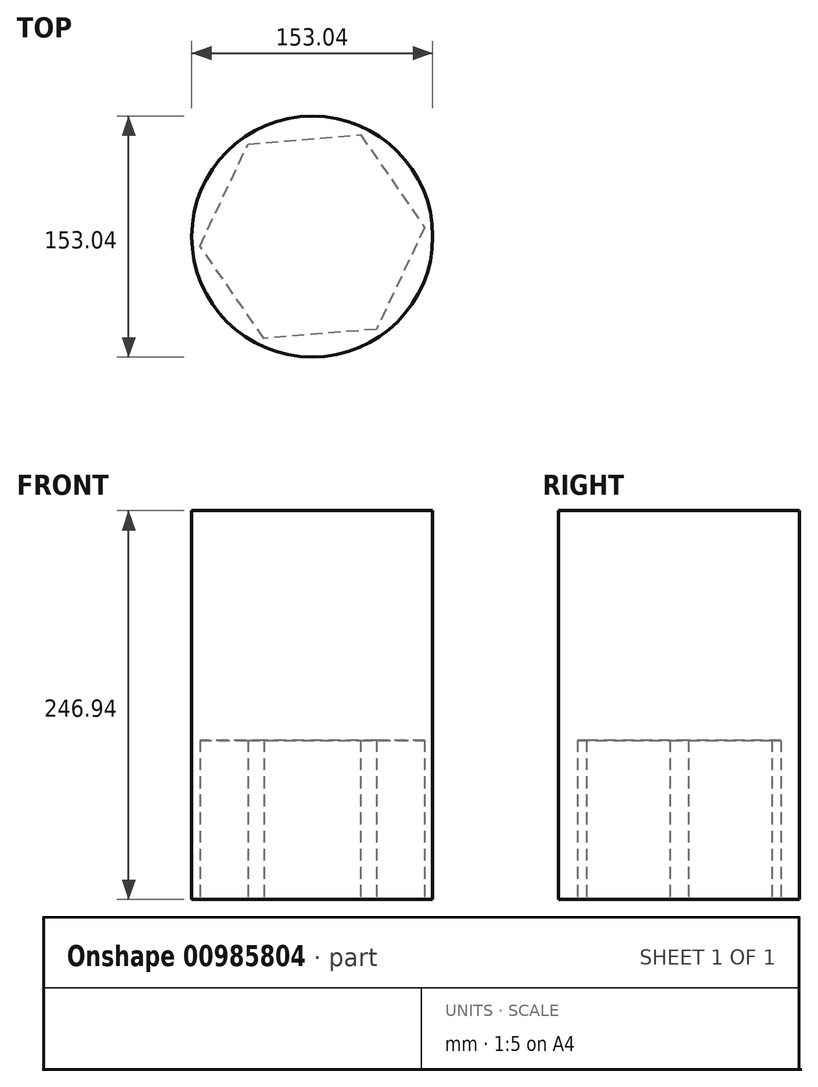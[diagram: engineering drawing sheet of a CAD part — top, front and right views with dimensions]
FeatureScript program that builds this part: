
annotation { "Feature Type Name" : "Feature", "Feature Type Description" : "" }
export const myFeature = defineFeature(function(context is Context, id is Id, definition is map)
    precondition{}
    {
        {
            var Q0;
            Q0=qCreatedBy(makeId("Top.planeOp"),FACE);
            var sketch = newSketch(context, id + "F0", { "sketchPlane" : qUnion([Q0])});
            skCircle(sketch, "E0", {"center": v(0, 0) * mm, "radius": 76.52 * mm});
            skSolve(sketch);
        }
        {
            var Q0;
            Q0=sQuery(id+"F0.wireOp",EDGE,"E0");
            extrude(context, id + "F1", {"bodyType" : ToolBodyType.SURFACE, "surfaceEntities" : qUnion([Q0]), "depth" : 57.15 * mm, "offsetDistance" : 25.4 * mm});
        }
        {
            var Q0;
            Q0=makeQuery(id+"F0.imprint","IMPRINT",FACE,{"disambiguationData":[TD([[makeQuery(id+"F0.imprint","IMPRINT",EDGE,{"derivedFrom":sQuery(id+"F0.wireOp",EDGE,"E0")}),1.0]])]});
            var sketch = newSketch(context, id + "F2", { "sketchPlane" : qUnion([Q0])});
            skCircle(sketch, "E1.cCircle", {"center": v(0, 0) * mm, "radius": 62.03 * mm, "construction": true});
            skLineSegment(sketch, "E1.0", {"start": v(-40.78, 58.89) * mm, "end": v(30.61, 64.76) * mm});
            skLineSegment(sketch, "E1.1", {"start": v(30.61, 64.76) * mm, "end": v(71.39, 5.87) * mm});
            skLineSegment(sketch, "E1.2", {"start": v(71.39, 5.87) * mm, "end": v(40.78, -58.89) * mm});
            skLineSegment(sketch, "E1.3", {"start": v(40.78, -58.89) * mm, "end": v(-30.61, -64.76) * mm});
            skLineSegment(sketch, "E1.4", {"start": v(-30.61, -64.76) * mm, "end": v(-71.39, -5.87) * mm});
            skLineSegment(sketch, "E1.5", {"start": v(-71.39, -5.87) * mm, "end": v(-40.78, 58.89) * mm});
            skPoint(sketch, "E1.0.midPoint", {"position": v(-5.08, 61.82) * mm});
            skSolve(sketch);
        }
        {
            var Q0;
            Q0=makeQuery(id+"F2.imprint","IMPRINT",FACE,{"disambiguationData":[TD([[makeQuery(id+"F2.imprint","IMPRINT",EDGE,{"derivedFrom":sQuery(id+"F2.wireOp",EDGE,"E1.0")}),-1.0]])]});
            extrude(context, id + "F3", {"entities" : qUnion([Q0]), "oppositeDirection" : true, "depth" : 61.72 * mm, "offsetDistance" : 25.4 * mm});
        }
        {
            var Q0;
            Q0=makeQuery(id+"F3.opExtrude","CAP_FACE",FACE,{"disambiguationData":[OSD([sQuery(id+"F2.wireOp",EDGE,"E1.0"),sQuery(id+"F2.wireOp",EDGE,"E1.1"),sQuery(id+"F2.wireOp",EDGE,"E1.2"),sQuery(id+"F2.wireOp",EDGE,"E1.3"),sQuery(id+"F2.wireOp",EDGE,"E1.4"),sQuery(id+"F2.wireOp",EDGE,"E1.5")])],"isStart":false});
            var sketch = newSketch(context, id + "F4", { "sketchPlane" : qUnion([Q0])});
            skCircle(sketch, "E2.cCircle", {"center": v(0, -2.43) * mm, "radius": 17.5 * mm, "construction": true});
            skLineSegment(sketch, "E2.0", {"start": v(-10.1, 15.07) * mm, "end": v(10.1, 15.07) * mm});
            skLineSegment(sketch, "E2.1", {"start": v(10.1, 15.07) * mm, "end": v(20.21, -2.43) * mm});
            skLineSegment(sketch, "E2.2", {"start": v(20.21, -2.43) * mm, "end": v(10.1, -19.93) * mm});
            skLineSegment(sketch, "E2.3", {"start": v(10.1, -19.93) * mm, "end": v(-10.1, -19.93) * mm});
            skLineSegment(sketch, "E2.4", {"start": v(-10.1, -19.93) * mm, "end": v(-20.21, -2.43) * mm});
            skLineSegment(sketch, "E2.5", {"start": v(-20.21, -2.43) * mm, "end": v(-10.1, 15.07) * mm});
            skPoint(sketch, "E2.0.midPoint", {"position": v(0, 15.07) * mm});
            skSolve(sketch);
        }
        {
            var Q0;
            Q0=makeQuery(id+"F4.imprint","IMPRINT",FACE,{"disambiguationData":[TD([[makeQuery(id+"F4.imprint","IMPRINT",EDGE,{"derivedFrom":sQuery(id+"F4.wireOp",EDGE,"E2.0")}),1.0]])]});
            var Q1;
            Q1=makeQuery(id+"F3.opExtrude","CAP_FACE",FACE,{"disambiguationData":[OSD([sQuery(id+"F2.wireOp",EDGE,"E1.0"),sQuery(id+"F2.wireOp",EDGE,"E1.1"),sQuery(id+"F2.wireOp",EDGE,"E1.2"),sQuery(id+"F2.wireOp",EDGE,"E1.3"),sQuery(id+"F2.wireOp",EDGE,"E1.4"),sQuery(id+"F2.wireOp",EDGE,"E1.5")])],"isStart":false});
            var Q2;
            Q2=makeQuery(id+"F0.imprint","IMPRINT",FACE,{"disambiguationData":[TD([[makeQuery(id+"F0.imprint","IMPRINT",EDGE,{"derivedFrom":sQuery(id+"F0.wireOp",EDGE,"E0")}),1.0]])]});
            var Q3;
            Q3=makeQuery(id+"F3.opExtrude","CAP_FACE",FACE,{"disambiguationData":[OSD([sQuery(id+"F2.wireOp",EDGE,"E1.0"),sQuery(id+"F2.wireOp",EDGE,"E1.1"),sQuery(id+"F2.wireOp",EDGE,"E1.2"),sQuery(id+"F2.wireOp",EDGE,"E1.3"),sQuery(id+"F2.wireOp",EDGE,"E1.4"),sQuery(id+"F2.wireOp",EDGE,"E1.5")])],"isStart":true});
            extrude(context, id + "F5", {"entities" : qUnion([Q0, Q1, Q2, Q3]), "operationType" : NewBodyOperationType.ADD, "endBound" : BoundingType.THROUGH_ALL, "depth" : 25.4 * mm, "offsetDistance" : 25.4 * mm});
        }
        {
            var Q0;
            {var subQ0=sQuery(id+"F2.wireOp",EDGE,"E1.5");var subQ1=sQuery(id+"F2.wireOp",EDGE,"E1.4");var subQ2=sQuery(id+"F2.wireOp",EDGE,"E1.3");var subQ3=sQuery(id+"F2.wireOp",EDGE,"E1.2");var subQ4=sQuery(id+"F2.wireOp",EDGE,"E1.1");var subQ5=sQuery(id+"F2.wireOp",EDGE,"E1.0");Q0=makeQuery(id+"F5.opExtrude","CAP_FACE",FACE,{"disambiguationData":[OSD([subQ5,subQ4,subQ3,subQ2,subQ1,subQ0]),TDD([makeQuery(id+"F3.opExtrude","CAP_FACE",FACE,{"disambiguationData":[OSD([subQ5,subQ4,subQ3,subQ2,subQ1,subQ0])],"isStart":false})])],"isStart":false});}
            extrude(context, id + "F6", {"entities" : qUnion([Q0]), "operationType" : NewBodyOperationType.REMOVE, "oppositeDirection" : true, "depth" : 162.8 * mm, "offsetDistance" : 25.4 * mm});
        }
    });
